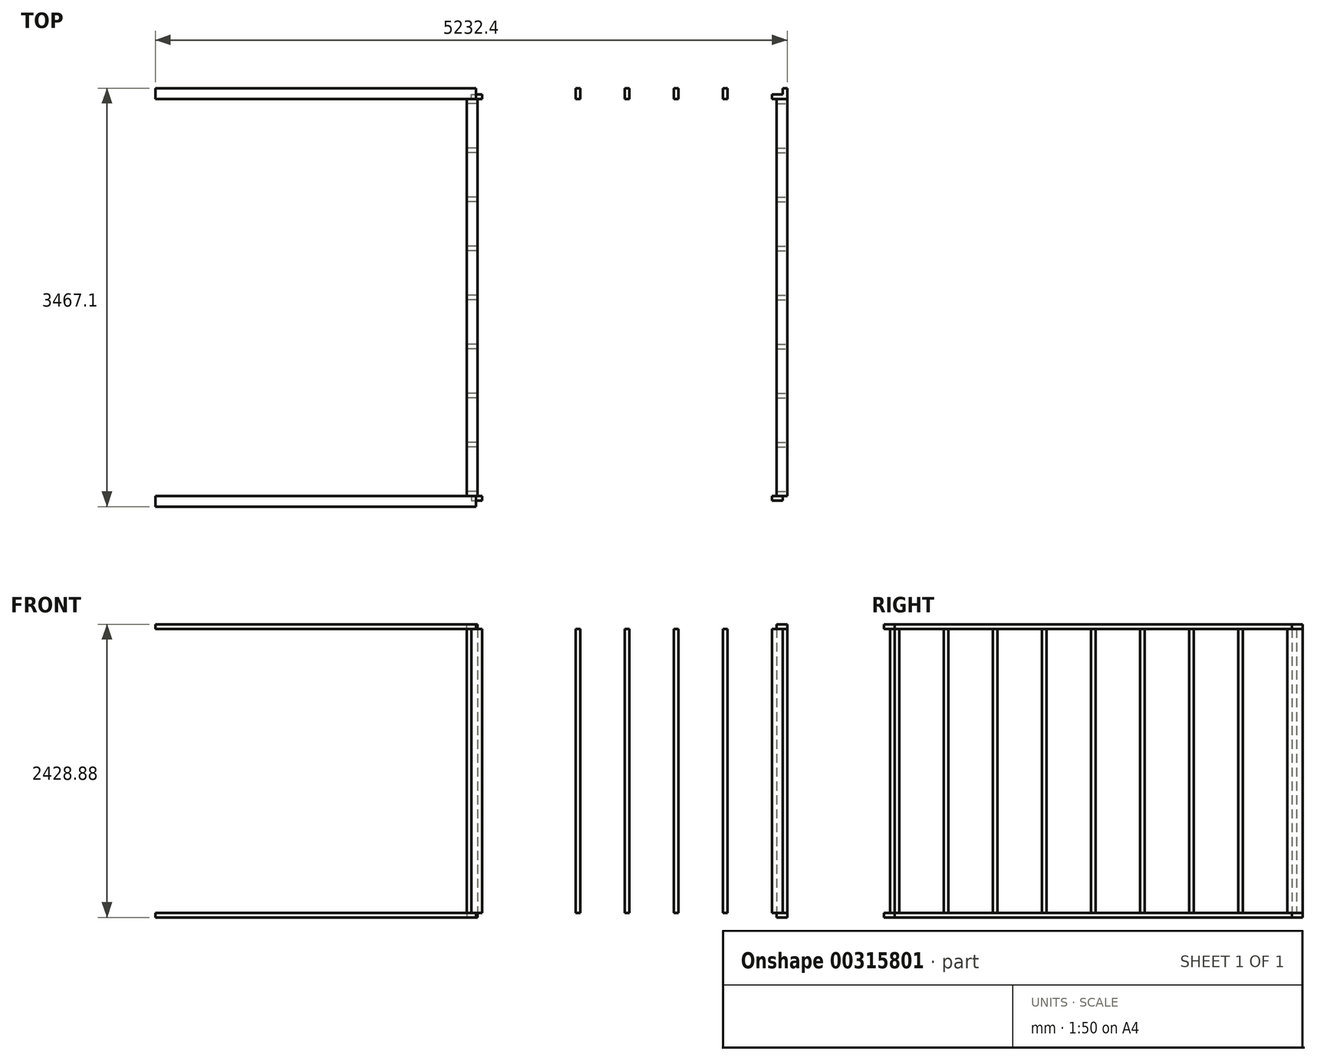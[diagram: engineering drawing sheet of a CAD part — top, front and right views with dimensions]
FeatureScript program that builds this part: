
annotation { "Feature Type Name" : "Feature", "Feature Type Description" : "" }
export const myFeature = defineFeature(function(context is Context, id is Id, definition is map)
    precondition{}
    {
        {
            var Q0;
            Q0=qCreatedBy(makeId("Top.planeOp"),FACE);
            var sketch = newSketch(context, id + "F0", { "sketchPlane" : qUnion([Q0])});
            skLineSegment(sketch, "E0.bottom", {"start": v(1238.25, -1644.65) * mm, "end": v(-1238.25, -1644.65) * mm});
            skLineSegment(sketch, "E0.top", {"start": v(1238.25, 1644.65) * mm, "end": v(-1238.25, 1644.65) * mm});
            skLineSegment(sketch, "E0.right", {"start": v(-1238.25, -1644.65) * mm, "end": v(-1238.25, 1644.65) * mm});
            skPoint(sketch, "E0.middle", {"position": v(0, 0) * mm});
            skLineSegment(sketch, "E1.bottom", {"start": v(-1238.25, 1644.65) * mm, "end": v(-1327.15, 1644.65) * mm});
            skLineSegment(sketch, "E1.top", {"start": v(-1238.25, 1606.55) * mm, "end": v(-1327.15, 1606.55) * mm});
            skLineSegment(sketch, "E1.left", {"start": v(-1238.25, 1644.65) * mm, "end": v(-1238.25, 1606.55) * mm});
            skLineSegment(sketch, "E1.right", {"start": v(-1327.15, 1644.65) * mm, "end": v(-1327.15, 1606.55) * mm});
            skLineSegment(sketch, "E2.1.0.0", {"start": v(-1238.25, 1238.25) * mm, "end": v(-1327.15, 1238.25) * mm});
            skLineSegment(sketch, "E2.1.0.1", {"start": v(-1238.25, 1238.25) * mm, "end": v(-1238.25, 1200.15) * mm});
            skLineSegment(sketch, "E2.1.0.2", {"start": v(-1238.25, 1200.15) * mm, "end": v(-1327.15, 1200.15) * mm});
            skLineSegment(sketch, "E2.1.0.3", {"start": v(-1327.15, 1238.25) * mm, "end": v(-1327.15, 1200.15) * mm});
            skLineSegment(sketch, "E2.2.0.0", {"start": v(-1238.25, 831.85) * mm, "end": v(-1327.15, 831.85) * mm});
            skLineSegment(sketch, "E2.2.0.1", {"start": v(-1238.25, 831.85) * mm, "end": v(-1238.25, 793.75) * mm});
            skLineSegment(sketch, "E2.2.0.2", {"start": v(-1238.25, 793.75) * mm, "end": v(-1327.15, 793.75) * mm});
            skLineSegment(sketch, "E2.2.0.3", {"start": v(-1327.15, 831.85) * mm, "end": v(-1327.15, 793.75) * mm});
            skLineSegment(sketch, "E2.3.0.0", {"start": v(-1238.25, 425.45) * mm, "end": v(-1327.15, 425.45) * mm});
            skLineSegment(sketch, "E2.3.0.1", {"start": v(-1238.25, 425.45) * mm, "end": v(-1238.25, 387.35) * mm});
            skLineSegment(sketch, "E2.3.0.2", {"start": v(-1238.25, 387.35) * mm, "end": v(-1327.15, 387.35) * mm});
            skLineSegment(sketch, "E2.3.0.3", {"start": v(-1327.15, 425.45) * mm, "end": v(-1327.15, 387.35) * mm});
            skLineSegment(sketch, "E2.4.0.0", {"start": v(-1238.25, 19.05) * mm, "end": v(-1327.15, 19.05) * mm});
            skLineSegment(sketch, "E2.4.0.1", {"start": v(-1238.25, 19.05) * mm, "end": v(-1238.25, -19.05) * mm});
            skLineSegment(sketch, "E2.4.0.2", {"start": v(-1238.25, -19.05) * mm, "end": v(-1327.15, -19.05) * mm});
            skLineSegment(sketch, "E2.4.0.3", {"start": v(-1327.15, 19.05) * mm, "end": v(-1327.15, -19.05) * mm});
            skLineSegment(sketch, "E2.5.0.0", {"start": v(-1238.25, -387.35) * mm, "end": v(-1327.15, -387.35) * mm});
            skLineSegment(sketch, "E2.5.0.1", {"start": v(-1238.25, -387.35) * mm, "end": v(-1238.25, -425.45) * mm});
            skLineSegment(sketch, "E2.5.0.2", {"start": v(-1238.25, -425.45) * mm, "end": v(-1327.15, -425.45) * mm});
            skLineSegment(sketch, "E2.5.0.3", {"start": v(-1327.15, -387.35) * mm, "end": v(-1327.15, -425.45) * mm});
            skLineSegment(sketch, "E2.6.0.0", {"start": v(-1238.25, -793.75) * mm, "end": v(-1327.15, -793.75) * mm});
            skLineSegment(sketch, "E2.6.0.1", {"start": v(-1238.25, -793.75) * mm, "end": v(-1238.25, -831.85) * mm});
            skLineSegment(sketch, "E2.6.0.2", {"start": v(-1238.25, -831.85) * mm, "end": v(-1327.15, -831.85) * mm});
            skLineSegment(sketch, "E2.6.0.3", {"start": v(-1327.15, -793.75) * mm, "end": v(-1327.15, -831.85) * mm});
            skLineSegment(sketch, "E2.7.0.0", {"start": v(-1238.25, -1200.15) * mm, "end": v(-1327.15, -1200.15) * mm});
            skLineSegment(sketch, "E2.7.0.1", {"start": v(-1238.25, -1200.15) * mm, "end": v(-1238.25, -1238.25) * mm});
            skLineSegment(sketch, "E2.7.0.2", {"start": v(-1238.25, -1238.25) * mm, "end": v(-1327.15, -1238.25) * mm});
            skLineSegment(sketch, "E2.7.0.3", {"start": v(-1327.15, -1200.15) * mm, "end": v(-1327.15, -1238.25) * mm});
            skLineSegment(sketch, "E2.8.0.0", {"start": v(-1238.25, -1606.55) * mm, "end": v(-1327.15, -1606.55) * mm});
            skLineSegment(sketch, "E2.8.0.1", {"start": v(-1238.25, -1606.55) * mm, "end": v(-1238.25, -1644.65) * mm});
            skLineSegment(sketch, "E2.8.0.2", {"start": v(-1238.25, -1644.65) * mm, "end": v(-1327.15, -1644.65) * mm});
            skLineSegment(sketch, "E2.8.0.3", {"start": v(-1327.15, -1606.55) * mm, "end": v(-1327.15, -1644.65) * mm});
            skLineSegment(sketch, "E2.direction1", {"start": v(-1327.15, 1644.65) * mm, "end": v(-1327.15, 1238.25) * mm, "construction": true});
            skLineSegment(sketch, "E3.bottom", {"start": v(-1327.15, -1644.65) * mm, "end": v(-1289.05, -1644.65) * mm});
            skLineSegment(sketch, "E3.top", {"start": v(-1327.15, -1733.55) * mm, "end": v(-1289.05, -1733.55) * mm});
            skLineSegment(sketch, "E3.left", {"start": v(-1327.15, -1644.65) * mm, "end": v(-1327.15, -1733.55) * mm});
            skLineSegment(sketch, "E3.right", {"start": v(-1289.05, -1644.65) * mm, "end": v(-1289.05, -1733.55) * mm});
            skLineSegment(sketch, "E4.bottom", {"start": v(-1289.05, -1644.65) * mm, "end": v(-1200.15, -1644.65) * mm});
            skLineSegment(sketch, "E4.top", {"start": v(-1289.05, -1682.75) * mm, "end": v(-1200.15, -1682.75) * mm});
            skLineSegment(sketch, "E4.left", {"start": v(-1289.05, -1644.65) * mm, "end": v(-1289.05, -1682.75) * mm});
            skLineSegment(sketch, "E4.right", {"start": v(-1200.15, -1644.65) * mm, "end": v(-1200.15, -1682.75) * mm});
            skLineSegment(sketch, "E5", {"start": v(-1289.05, -1644.65) * mm, "end": v(-882.65, -1644.65) * mm});
            skLineSegment(sketch, "E6", {"start": v(-1238.25, 1625.6) * mm, "end": v(-1238.25, -1625.6) * mm});
            skLineSegment(sketch, "E7.bottom", {"start": v(1238.25, 1644.65) * mm, "end": v(1327.15, 1644.65) * mm});
            skLineSegment(sketch, "E7.top", {"start": v(1238.25, 1606.55) * mm, "end": v(1327.15, 1606.55) * mm});
            skLineSegment(sketch, "E7.left", {"start": v(1238.25, 1644.65) * mm, "end": v(1238.25, 1606.55) * mm});
            skLineSegment(sketch, "E7.right", {"start": v(1327.15, 1644.65) * mm, "end": v(1327.15, 1606.55) * mm});
            skLineSegment(sketch, "E8.bottom", {"start": v(1238.25, -1644.65) * mm, "end": v(1327.15, -1644.65) * mm});
            skLineSegment(sketch, "E8.top", {"start": v(1238.25, -1606.55) * mm, "end": v(1327.15, -1606.55) * mm});
            skLineSegment(sketch, "E8.left", {"start": v(1238.25, -1644.65) * mm, "end": v(1238.25, -1606.55) * mm});
            skLineSegment(sketch, "E8.right", {"start": v(1327.15, -1644.65) * mm, "end": v(1327.15, -1606.55) * mm});
            skLineSegment(sketch, "E9.bottom", {"start": v(1327.15, -1644.65) * mm, "end": v(1289.05, -1644.65) * mm});
            skLineSegment(sketch, "E9.top", {"start": v(1327.15, -1733.55) * mm, "end": v(1289.05, -1733.55) * mm});
            skLineSegment(sketch, "E9.left", {"start": v(1327.15, -1644.65) * mm, "end": v(1327.15, -1733.55) * mm});
            skLineSegment(sketch, "E9.right", {"start": v(1289.05, -1644.65) * mm, "end": v(1289.05, -1733.55) * mm});
            skLineSegment(sketch, "E10.bottom", {"start": v(1289.05, -1644.65) * mm, "end": v(1200.15, -1644.65) * mm});
            skLineSegment(sketch, "E10.top", {"start": v(1289.05, -1682.75) * mm, "end": v(1200.15, -1682.75) * mm});
            skLineSegment(sketch, "E10.left", {"start": v(1289.05, -1644.65) * mm, "end": v(1289.05, -1682.75) * mm});
            skLineSegment(sketch, "E10.right", {"start": v(1200.15, -1644.65) * mm, "end": v(1200.15, -1682.75) * mm});
            skLineSegment(sketch, "E11", {"start": v(1289.05, -1644.65) * mm, "end": v(904.68, -1644.65) * mm});
            skLineSegment(sketch, "E12", {"start": v(904.68, -1644.65) * mm, "end": v(1289.05, -1644.65) * mm});
            skLineSegment(sketch, "E13.bottom", {"start": v(-1327.15, 1644.65) * mm, "end": v(-1289.05, 1644.65) * mm});
            skLineSegment(sketch, "E13.top", {"start": v(-1327.15, 1733.55) * mm, "end": v(-1289.05, 1733.55) * mm});
            skLineSegment(sketch, "E13.left", {"start": v(-1327.15, 1644.65) * mm, "end": v(-1327.15, 1733.55) * mm});
            skLineSegment(sketch, "E13.right", {"start": v(-1289.05, 1644.65) * mm, "end": v(-1289.05, 1733.55) * mm});
            skLineSegment(sketch, "E14.bottom", {"start": v(-1289.05, 1644.65) * mm, "end": v(-1200.15, 1644.65) * mm});
            skLineSegment(sketch, "E14.top", {"start": v(-1289.05, 1682.75) * mm, "end": v(-1200.15, 1682.75) * mm});
            skLineSegment(sketch, "E14.left", {"start": v(-1289.05, 1644.65) * mm, "end": v(-1289.05, 1682.75) * mm});
            skLineSegment(sketch, "E14.right", {"start": v(-1200.15, 1644.65) * mm, "end": v(-1200.15, 1682.75) * mm});
            skLineSegment(sketch, "E15", {"start": v(-1200.15, 1644.65) * mm, "end": v(-831.85, 1644.65) * mm});
            skLineSegment(sketch, "E16.bottom", {"start": v(-831.85, 1644.65) * mm, "end": v(-793.75, 1644.65) * mm});
            skLineSegment(sketch, "E16.top", {"start": v(-831.85, 1733.55) * mm, "end": v(-793.75, 1733.55) * mm});
            skLineSegment(sketch, "E16.left", {"start": v(-831.85, 1644.65) * mm, "end": v(-831.85, 1733.55) * mm});
            skLineSegment(sketch, "E16.right", {"start": v(-793.75, 1644.65) * mm, "end": v(-793.75, 1733.55) * mm});
            skLineSegment(sketch, "E17.1.0.0", {"start": v(-387.35, 1644.65) * mm, "end": v(-387.35, 1733.55) * mm});
            skLineSegment(sketch, "E17.1.0.1", {"start": v(-425.45, 1733.55) * mm, "end": v(-387.35, 1733.55) * mm});
            skLineSegment(sketch, "E17.1.0.2", {"start": v(-425.45, 1644.65) * mm, "end": v(-425.45, 1733.55) * mm});
            skLineSegment(sketch, "E17.2.0.0", {"start": v(19.05, 1644.65) * mm, "end": v(19.05, 1733.55) * mm});
            skLineSegment(sketch, "E17.2.0.1", {"start": v(-19.05, 1733.55) * mm, "end": v(19.05, 1733.55) * mm});
            skLineSegment(sketch, "E17.2.0.2", {"start": v(-19.05, 1644.65) * mm, "end": v(-19.05, 1733.55) * mm});
            skLineSegment(sketch, "E17.3.0.0", {"start": v(425.45, 1644.65) * mm, "end": v(425.45, 1733.55) * mm});
            skLineSegment(sketch, "E17.3.0.1", {"start": v(387.35, 1733.55) * mm, "end": v(425.45, 1733.55) * mm});
            skLineSegment(sketch, "E17.3.0.2", {"start": v(387.35, 1644.65) * mm, "end": v(387.35, 1733.55) * mm});
            skLineSegment(sketch, "E17.4.0.0", {"start": v(831.85, 1644.65) * mm, "end": v(831.85, 1733.55) * mm});
            skLineSegment(sketch, "E17.4.0.1", {"start": v(793.75, 1733.55) * mm, "end": v(831.85, 1733.55) * mm});
            skLineSegment(sketch, "E17.4.0.2", {"start": v(793.75, 1644.65) * mm, "end": v(793.75, 1733.55) * mm});
            skLineSegment(sketch, "E17.direction1", {"start": v(-793.75, 1644.65) * mm, "end": v(-387.35, 1644.65) * mm, "construction": true});
            skLineSegment(sketch, "E18.bottom", {"start": v(1327.15, 1644.65) * mm, "end": v(1282.7, 1644.65) * mm});
            skLineSegment(sketch, "E18.left", {"start": v(1327.15, 1644.65) * mm, "end": v(1327.15, 1733.55) * mm});
            skLineSegment(sketch, "E19", {"start": v(1327.15, 1733.55) * mm, "end": v(1289.05, 1733.55) * mm});
            skLineSegment(sketch, "E20", {"start": v(1289.05, 1733.55) * mm, "end": v(1289.05, 1644.65) * mm});
            skLineSegment(sketch, "E21", {"start": v(1289.05, 1644.65) * mm, "end": v(1327.15, 1644.65) * mm});
            skLineSegment(sketch, "E22.bottom", {"start": v(1289.05, 1644.65) * mm, "end": v(1200.15, 1644.65) * mm});
            skLineSegment(sketch, "E22.top", {"start": v(1289.05, 1682.75) * mm, "end": v(1200.15, 1682.75) * mm});
            skLineSegment(sketch, "E22.left", {"start": v(1289.05, 1644.65) * mm, "end": v(1289.05, 1682.75) * mm});
            skLineSegment(sketch, "E22.right", {"start": v(1200.15, 1644.65) * mm, "end": v(1200.15, 1682.75) * mm});
            skLineSegment(sketch, "E23", {"start": v(831.85, 1644.65) * mm, "end": v(1238.25, 1644.65) * mm});
            skLineSegment(sketch, "E24", {"start": v(1238.25, -1644.65) * mm, "end": v(1238.25, 1644.65) * mm});
            skLineSegment(sketch, "E25", {"start": v(0, 0) * mm, "end": v(0, 279.47) * mm});
            skLineSegment(sketch, "E26.MirrorCS", {"start": v(1327.15, 1238.25) * mm, "end": v(1327.15, 1200.15) * mm});
            skLineSegment(sketch, "E27.MirrorCS", {"start": v(1327.15, -793.75) * mm, "end": v(1327.15, -831.85) * mm});
            skLineSegment(sketch, "E28.MirrorCS", {"start": v(1327.15, 19.05) * mm, "end": v(1327.15, -19.05) * mm});
            skLineSegment(sketch, "E29.MirrorCS", {"start": v(1238.25, 793.75) * mm, "end": v(1327.15, 793.75) * mm});
            skLineSegment(sketch, "E30.MirrorCS", {"start": v(1327.15, 831.85) * mm, "end": v(1327.15, 793.75) * mm});
            skLineSegment(sketch, "E31.MirrorCS", {"start": v(1327.15, -387.35) * mm, "end": v(1327.15, -425.45) * mm});
            skLineSegment(sketch, "E32.MirrorCS", {"start": v(1238.25, 19.05) * mm, "end": v(1327.15, 19.05) * mm});
            skLineSegment(sketch, "E33.MirrorCS", {"start": v(1238.25, 831.85) * mm, "end": v(1238.25, 793.75) * mm});
            skLineSegment(sketch, "E34.MirrorCS", {"start": v(1238.25, -1200.15) * mm, "end": v(1327.15, -1200.15) * mm});
            skLineSegment(sketch, "E35.MirrorCS", {"start": v(1238.25, -793.75) * mm, "end": v(1238.25, -831.85) * mm});
            skLineSegment(sketch, "E36.MirrorCS", {"start": v(1238.25, 425.45) * mm, "end": v(1327.15, 425.45) * mm});
            skLineSegment(sketch, "E37.MirrorCS", {"start": v(1238.25, 1238.25) * mm, "end": v(1327.15, 1238.25) * mm});
            skLineSegment(sketch, "E38.MirrorCS", {"start": v(1238.25, 1238.25) * mm, "end": v(1238.25, 1200.15) * mm});
            skLineSegment(sketch, "E39.MirrorCS", {"start": v(1238.25, 387.35) * mm, "end": v(1327.15, 387.35) * mm});
            skLineSegment(sketch, "E40.MirrorCS", {"start": v(1238.25, 1200.15) * mm, "end": v(1327.15, 1200.15) * mm});
            skLineSegment(sketch, "E41.MirrorCS", {"start": v(1238.25, -387.35) * mm, "end": v(1238.25, -425.45) * mm});
            skLineSegment(sketch, "E42.MirrorCS", {"start": v(1238.25, -1200.15) * mm, "end": v(1238.25, -1238.25) * mm});
            skLineSegment(sketch, "E43.MirrorCS", {"start": v(1238.25, -793.75) * mm, "end": v(1327.15, -793.75) * mm});
            skLineSegment(sketch, "E44.MirrorCS", {"start": v(1238.25, -1238.25) * mm, "end": v(1327.15, -1238.25) * mm});
            skLineSegment(sketch, "E45.MirrorCS", {"start": v(1238.25, -19.05) * mm, "end": v(1327.15, -19.05) * mm});
            skLineSegment(sketch, "E46.MirrorCS", {"start": v(1238.25, 831.85) * mm, "end": v(1327.15, 831.85) * mm});
            skLineSegment(sketch, "E47.MirrorCS", {"start": v(1238.25, -387.35) * mm, "end": v(1327.15, -387.35) * mm});
            skLineSegment(sketch, "E48.MirrorCS", {"start": v(1238.25, -831.85) * mm, "end": v(1327.15, -831.85) * mm});
            skLineSegment(sketch, "E49.MirrorCS", {"start": v(1238.25, 425.45) * mm, "end": v(1238.25, 387.35) * mm});
            skLineSegment(sketch, "E50.MirrorCS", {"start": v(1327.15, 425.45) * mm, "end": v(1327.15, 387.35) * mm});
            skLineSegment(sketch, "E51.MirrorCS", {"start": v(1238.25, 19.05) * mm, "end": v(1238.25, -19.05) * mm});
            skLineSegment(sketch, "E52.MirrorCS", {"start": v(1327.15, -1200.15) * mm, "end": v(1327.15, -1238.25) * mm});
            skLineSegment(sketch, "E53.MirrorCS", {"start": v(1238.25, -425.45) * mm, "end": v(1327.15, -425.45) * mm});
            skSolve(sketch);
        }
        {
            var Q0;
            {var subQ1=sQuery(id+"F0.wireOp",EDGE,"E1.top");Q0=makeQuery(id+"F0.imprint","IMPRINT",FACE,{"disambiguationData":[TD([[makeQuery(id+"F0.imprint","IMPRINT",EDGE,{"derivedFrom":subQ1}),-1.0]])]});}
            var Q1;
            Q1=makeQuery(id+"F0.imprint","IMPRINT",FACE,{"disambiguationData":[TD([[makeQuery(id+"F0.imprint","IMPRINT",EDGE,{"derivedFrom":sQuery(id+"F0.wireOp",EDGE,"E13.bottom")}),1.0]])]});
            var Q2;
            Q2=makeQuery(id+"F0.imprint","IMPRINT",FACE,{"disambiguationData":[TD([[makeQuery(id+"F0.imprint","IMPRINT",EDGE,{"derivedFrom":sQuery(id+"F0.wireOp",EDGE,"E14.top")}),-1.0]])]});
            var Q3;
            Q3=makeQuery(id+"F0.imprint","IMPRINT",FACE,{"disambiguationData":[TD([[makeQuery(id+"F0.imprint","IMPRINT",EDGE,{"derivedFrom":sQuery(id+"F0.wireOp",EDGE,"E16.bottom")}),1.0]])]});
            var Q4;
            {var subQ0=sQuery(id+"F0.wireOp",EDGE,"E17.1.0.0");Q4=makeQuery(id+"F0.imprint","IMPRINT",FACE,{"disambiguationData":[TD([[makeQuery(id+"F0.imprint","IMPRINT",EDGE,{"derivedFrom":subQ0}),1.0]])]});}
            var Q5;
            {var subQ0=sQuery(id+"F0.wireOp",EDGE,"E17.2.0.0");Q5=makeQuery(id+"F0.imprint","IMPRINT",FACE,{"disambiguationData":[TD([[makeQuery(id+"F0.imprint","IMPRINT",EDGE,{"derivedFrom":subQ0}),1.0]])]});}
            var Q6;
            {var subQ0=sQuery(id+"F0.wireOp",EDGE,"E17.3.0.0");Q6=makeQuery(id+"F0.imprint","IMPRINT",FACE,{"disambiguationData":[TD([[makeQuery(id+"F0.imprint","IMPRINT",EDGE,{"derivedFrom":subQ0}),1.0]])]});}
            var Q7;
            Q7=makeQuery(id+"F0.imprint","IMPRINT",FACE,{"disambiguationData":[TD([[makeQuery(id+"F0.imprint","IMPRINT",EDGE,{"derivedFrom":sQuery(id+"F0.wireOp",EDGE,"E22.top")}),1.0]])]});
            var Q8;
            Q8=makeQuery(id+"F0.imprint","IMPRINT",FACE,{"disambiguationData":[TD([[makeQuery(id+"F0.imprint","IMPRINT",EDGE,{"derivedFrom":sQuery(id+"F0.wireOp",EDGE,"E18.left")}),1.0]])]});
            var Q9;
            {var subQ3=sQuery(id+"F0.wireOp",EDGE,"E7.top");Q9=makeQuery(id+"F0.imprint","IMPRINT",FACE,{"disambiguationData":[TD([[makeQuery(id+"F0.imprint","IMPRINT",EDGE,{"derivedFrom":subQ3}),1.0]])]});}
            var Q10;
            Q10=makeQuery(id+"F0.imprint","IMPRINT",FACE,{"disambiguationData":[TD([[makeQuery(id+"F0.imprint","IMPRINT",EDGE,{"derivedFrom":sQuery(id+"F0.wireOp",EDGE,"E26.MirrorCS")}),-1.0]])]});
            var Q11;
            Q11=makeQuery(id+"F0.imprint","IMPRINT",FACE,{"disambiguationData":[TD([[makeQuery(id+"F0.imprint","IMPRINT",EDGE,{"derivedFrom":sQuery(id+"F0.wireOp",EDGE,"E29.MirrorCS")}),1.0]])]});
            var Q12;
            Q12=makeQuery(id+"F0.imprint","IMPRINT",FACE,{"disambiguationData":[TD([[makeQuery(id+"F0.imprint","IMPRINT",EDGE,{"derivedFrom":sQuery(id+"F0.wireOp",EDGE,"E36.MirrorCS")}),-1.0]])]});
            var Q13;
            Q13=makeQuery(id+"F0.imprint","IMPRINT",FACE,{"disambiguationData":[TD([[makeQuery(id+"F0.imprint","IMPRINT",EDGE,{"derivedFrom":sQuery(id+"F0.wireOp",EDGE,"E28.MirrorCS")}),-1.0]])]});
            var Q14;
            Q14=makeQuery(id+"F0.imprint","IMPRINT",FACE,{"disambiguationData":[TD([[makeQuery(id+"F0.imprint","IMPRINT",EDGE,{"derivedFrom":sQuery(id+"F0.wireOp",EDGE,"E31.MirrorCS")}),-1.0]])]});
            var Q15;
            Q15=makeQuery(id+"F0.imprint","IMPRINT",FACE,{"disambiguationData":[TD([[makeQuery(id+"F0.imprint","IMPRINT",EDGE,{"derivedFrom":sQuery(id+"F0.wireOp",EDGE,"E27.MirrorCS")}),-1.0]])]});
            var Q16;
            Q16=makeQuery(id+"F0.imprint","IMPRINT",FACE,{"disambiguationData":[TD([[makeQuery(id+"F0.imprint","IMPRINT",EDGE,{"derivedFrom":sQuery(id+"F0.wireOp",EDGE,"E34.MirrorCS")}),-1.0]])]});
            var Q17;
            {var subQ4=sQuery(id+"F0.wireOp",EDGE,"E8.top");Q17=makeQuery(id+"F0.imprint","IMPRINT",FACE,{"disambiguationData":[TD([[makeQuery(id+"F0.imprint","IMPRINT",EDGE,{"derivedFrom":subQ4}),-1.0]])]});}
            var Q18;
            Q18=makeQuery(id+"F0.imprint","IMPRINT",FACE,{"disambiguationData":[TD([[makeQuery(id+"F0.imprint","IMPRINT",EDGE,{"derivedFrom":sQuery(id+"F0.wireOp",EDGE,"E10.top")}),-1.0]])]});
            var Q19;
            Q19=makeQuery(id+"F0.imprint","IMPRINT",FACE,{"disambiguationData":[TD([[makeQuery(id+"F0.imprint","IMPRINT",EDGE,{"derivedFrom":sQuery(id+"F0.wireOp",EDGE,"E9.bottom")}),1.0]])]});
            var Q20;
            Q20=makeQuery(id+"F0.imprint","IMPRINT",FACE,{"disambiguationData":[TD([[makeQuery(id+"F0.imprint","IMPRINT",EDGE,{"derivedFrom":sQuery(id+"F0.wireOp",EDGE,"E4.top")}),1.0]])]});
            var Q21;
            Q21=makeQuery(id+"F0.imprint","IMPRINT",FACE,{"disambiguationData":[TD([[makeQuery(id+"F0.imprint","IMPRINT",EDGE,{"derivedFrom":sQuery(id+"F0.wireOp",EDGE,"E3.bottom")}),-1.0]])]});
            var Q22;
            {var subQ3=sQuery(id+"F0.wireOp",EDGE,"E2.8.0.0");Q22=makeQuery(id+"F0.imprint","IMPRINT",FACE,{"disambiguationData":[TD([[makeQuery(id+"F0.imprint","IMPRINT",EDGE,{"derivedFrom":subQ3}),1.0]])]});}
            var Q23;
            {var subQ0=sQuery(id+"F0.wireOp",EDGE,"E2.7.0.0");Q23=makeQuery(id+"F0.imprint","IMPRINT",FACE,{"disambiguationData":[TD([[makeQuery(id+"F0.imprint","IMPRINT",EDGE,{"derivedFrom":subQ0}),1.0]])]});}
            var Q24;
            {var subQ0=sQuery(id+"F0.wireOp",EDGE,"E2.6.0.0");Q24=makeQuery(id+"F0.imprint","IMPRINT",FACE,{"disambiguationData":[TD([[makeQuery(id+"F0.imprint","IMPRINT",EDGE,{"derivedFrom":subQ0}),1.0]])]});}
            var Q25;
            {var subQ0=sQuery(id+"F0.wireOp",EDGE,"E2.5.0.0");Q25=makeQuery(id+"F0.imprint","IMPRINT",FACE,{"disambiguationData":[TD([[makeQuery(id+"F0.imprint","IMPRINT",EDGE,{"derivedFrom":subQ0}),1.0]])]});}
            var Q26;
            {var subQ0=sQuery(id+"F0.wireOp",EDGE,"E2.4.0.0");Q26=makeQuery(id+"F0.imprint","IMPRINT",FACE,{"disambiguationData":[TD([[makeQuery(id+"F0.imprint","IMPRINT",EDGE,{"derivedFrom":subQ0}),1.0]])]});}
            var Q27;
            {var subQ0=sQuery(id+"F0.wireOp",EDGE,"E2.3.0.0");Q27=makeQuery(id+"F0.imprint","IMPRINT",FACE,{"disambiguationData":[TD([[makeQuery(id+"F0.imprint","IMPRINT",EDGE,{"derivedFrom":subQ0}),1.0]])]});}
            var Q28;
            {var subQ0=sQuery(id+"F0.wireOp",EDGE,"E2.2.0.0");Q28=makeQuery(id+"F0.imprint","IMPRINT",FACE,{"disambiguationData":[TD([[makeQuery(id+"F0.imprint","IMPRINT",EDGE,{"derivedFrom":subQ0}),1.0]])]});}
            var Q29;
            {var subQ0=sQuery(id+"F0.wireOp",EDGE,"E2.1.0.0");Q29=makeQuery(id+"F0.imprint","IMPRINT",FACE,{"disambiguationData":[TD([[makeQuery(id+"F0.imprint","IMPRINT",EDGE,{"derivedFrom":subQ0}),1.0]])]});}
            var Q30;
            {var subQ0=sQuery(id+"F0.wireOp",EDGE,"E17.4.0.0");Q30=makeQuery(id+"F0.imprint","IMPRINT",FACE,{"disambiguationData":[TD([[makeQuery(id+"F0.imprint","IMPRINT",EDGE,{"derivedFrom":subQ0}),1.0]])]});}
            extrude(context, id + "F1", {"entities" : qUnion([Q0, Q1, Q2, Q3, Q4, Q5, Q6, Q7, Q8, Q9, Q10, Q11, Q12, Q13, Q14, Q15, Q16, Q17, Q18, Q19, Q20, Q21, Q22, Q23, Q24, Q25, Q26, Q27, Q28, Q29, Q30]), "depth" : 2352.67 * mm});
        }
        {
            var Q0;
            Q0=makeQuery(id+"F1.opExtrude","SWEPT_FACE",FACE,{"disambiguationData":[OSD([sQuery(id+"F0.wireOp",EDGE,"E8.top")])]});
            var sketch = newSketch(context, id + "F2", { "sketchPlane" : qUnion([Q0])});
            skLineSegment(sketch, "E54.bottom", {"start": v(-1327.15, 0) * mm, "end": v(-1238.25, 0) * mm});
            skLineSegment(sketch, "E54.top", {"start": v(-1327.15, -38.1) * mm, "end": v(-1238.25, -38.1) * mm});
            skLineSegment(sketch, "E54.left", {"start": v(-1327.15, 0) * mm, "end": v(-1327.15, -38.1) * mm});
            skLineSegment(sketch, "E54.right", {"start": v(-1238.25, 0) * mm, "end": v(-1238.25, -38.1) * mm});
            skSolve(sketch);
        }
        {
            var Q0;
            Q0=makeQuery(id+"F2.imprint","IMPRINT",FACE,{"disambiguationData":[TD([[makeQuery(id+"F2.imprint","IMPRINT",EDGE,{"derivedFrom":sQuery(id+"F2.wireOp",EDGE,"E54.bottom")}),1.0]])]});
            extrude(context, id + "F3", {"entities" : qUnion([Q0]), "depth" : 3251.2 * mm, "hasSecondDirection" : true, "secondDirectionOppositeDirection" : true, "secondDirectionDepth" : 38.1 * mm});
        }
        {
            var Q0;
            Q0=makeQuery(id+"F1.opExtrude","SWEPT_FACE",FACE,{"disambiguationData":[OSD([sQuery(id+"F0.wireOp",EDGE,"E1.top")])]});
            var sketch = newSketch(context, id + "F4", { "sketchPlane" : qUnion([Q0])});
            skLineSegment(sketch, "E55.bottom", {"start": v(-1327.15, 0) * mm, "end": v(-1238.25, 0) * mm});
            skLineSegment(sketch, "E55.top", {"start": v(-1327.15, -38.1) * mm, "end": v(-1238.25, -38.1) * mm});
            skLineSegment(sketch, "E55.left", {"start": v(-1327.15, 0) * mm, "end": v(-1327.15, -38.1) * mm});
            skLineSegment(sketch, "E55.right", {"start": v(-1238.25, 0) * mm, "end": v(-1238.25, -38.1) * mm});
            skSolve(sketch);
        }
        {
            var Q0;
            Q0=makeQuery(id+"F4.imprint","IMPRINT",FACE,{"disambiguationData":[TD([[makeQuery(id+"F4.imprint","IMPRINT",EDGE,{"derivedFrom":sQuery(id+"F4.wireOp",EDGE,"E55.bottom")}),1.0]])]});
            extrude(context, id + "F5", {"entities" : qUnion([Q0]), "depth" : 3251.2 * mm, "hasSecondDirection" : true, "secondDirectionOppositeDirection" : true, "secondDirectionDepth" : 38.1 * mm});
        }
        {
            var Q0;
            Q0=makeQuery(id+"F1.opExtrude","SWEPT_FACE",FACE,{"disambiguationData":[OSD([sQuery(id+"F0.wireOp",EDGE,"E3.right")])]});
            var sketch = newSketch(context, id + "F6", { "sketchPlane" : qUnion([Q0])});
            skLineSegment(sketch, "E56.bottom", {"start": v(-1733.55, 0) * mm, "end": v(-1644.65, 0) * mm});
            skLineSegment(sketch, "E56.top", {"start": v(-1733.55, -38.1) * mm, "end": v(-1644.65, -38.1) * mm});
            skLineSegment(sketch, "E56.left", {"start": v(-1733.55, 0) * mm, "end": v(-1733.55, -38.1) * mm});
            skLineSegment(sketch, "E56.right", {"start": v(-1644.65, 0) * mm, "end": v(-1644.65, -38.1) * mm});
            skSolve(sketch);
        }
        {
            var Q0;
            Q0=makeQuery(id+"F6.imprint","IMPRINT",FACE,{"disambiguationData":[TD([[makeQuery(id+"F6.imprint","IMPRINT",EDGE,{"derivedFrom":sQuery(id+"F6.wireOp",EDGE,"E56.top")}),1.0]])]});
            extrude(context, id + "F7", {"entities" : qUnion([Q0]), "depth" : 2616.2 * mm, "hasSecondDirection" : true, "secondDirectionOppositeDirection" : true, "secondDirectionDepth" : 38.1 * mm});
        }
        {
            var Q0;
            Q0=makeQuery(id+"F1.opExtrude","SWEPT_FACE",FACE,{"disambiguationData":[OSD([sQuery(id+"F0.wireOp",EDGE,"E13.right")])]});
            var sketch = newSketch(context, id + "F8", { "sketchPlane" : qUnion([Q0])});
            skLineSegment(sketch, "E57.bottom", {"start": v(1733.55, 0) * mm, "end": v(1644.65, 0) * mm});
            skLineSegment(sketch, "E57.top", {"start": v(1733.55, -38.1) * mm, "end": v(1644.65, -38.1) * mm});
            skLineSegment(sketch, "E57.left", {"start": v(1733.55, 0) * mm, "end": v(1733.55, -38.1) * mm});
            skLineSegment(sketch, "E57.right", {"start": v(1644.65, 0) * mm, "end": v(1644.65, -38.1) * mm});
            skSolve(sketch);
        }
        {
            var Q0;
            Q0=makeQuery(id+"F8.imprint","IMPRINT",FACE,{"disambiguationData":[TD([[makeQuery(id+"F8.imprint","IMPRINT",EDGE,{"derivedFrom":sQuery(id+"F8.wireOp",EDGE,"E57.top")}),-1.0]])]});
            extrude(context, id + "F9", {"entities" : qUnion([Q0]), "depth" : 2616.2 * mm, "hasSecondDirection" : true, "secondDirectionOppositeDirection" : true, "secondDirectionDepth" : 38.1 * mm});
        }
        {
            var Q0;
            Q0=makeQuery(id+"F1.opExtrude","SWEPT_FACE",FACE,{"disambiguationData":[OSD([sQuery(id+"F0.wireOp",EDGE,"E7.top")])]});
            var sketch = newSketch(context, id + "F10", { "sketchPlane" : qUnion([Q0])});
            skLineSegment(sketch, "E58.bottom", {"start": v(1238.25, 2352.68) * mm, "end": v(1327.15, 2352.68) * mm});
            skLineSegment(sketch, "E58.top", {"start": v(1238.25, 2390.78) * mm, "end": v(1327.15, 2390.78) * mm});
            skLineSegment(sketch, "E58.left", {"start": v(1238.25, 2352.68) * mm, "end": v(1238.25, 2390.78) * mm});
            skLineSegment(sketch, "E58.right", {"start": v(1327.15, 2352.68) * mm, "end": v(1327.15, 2390.78) * mm});
            skSolve(sketch);
        }
        {
            var Q0;
            Q0=makeQuery(id+"F10.imprint","IMPRINT",FACE,{"disambiguationData":[TD([[makeQuery(id+"F10.imprint","IMPRINT",EDGE,{"derivedFrom":sQuery(id+"F10.wireOp",EDGE,"E58.bottom")}),1.0]])]});
            extrude(context, id + "F11", {"entities" : qUnion([Q0]), "depth" : 3251.2 * mm, "hasSecondDirection" : true, "secondDirectionOppositeDirection" : true, "secondDirectionDepth" : 38.1 * mm});
        }
        {
            var Q0;
            Q0=makeQuery(id+"F1.opExtrude","SWEPT_FACE",FACE,{"disambiguationData":[OSD([sQuery(id+"F0.wireOp",EDGE,"E1.top")])]});
            var sketch = newSketch(context, id + "F12", { "sketchPlane" : qUnion([Q0])});
            skLineSegment(sketch, "E59.bottom", {"start": v(-1327.15, 2352.68) * mm, "end": v(-1238.25, 2352.68) * mm});
            skLineSegment(sketch, "E59.top", {"start": v(-1327.15, 2390.78) * mm, "end": v(-1238.25, 2390.78) * mm});
            skLineSegment(sketch, "E59.left", {"start": v(-1327.15, 2352.68) * mm, "end": v(-1327.15, 2390.78) * mm});
            skLineSegment(sketch, "E59.right", {"start": v(-1238.25, 2352.68) * mm, "end": v(-1238.25, 2390.78) * mm});
            skSolve(sketch);
        }
        {
            var Q0;
            Q0=makeQuery(id+"F12.imprint","IMPRINT",FACE,{"disambiguationData":[TD([[makeQuery(id+"F12.imprint","IMPRINT",EDGE,{"derivedFrom":sQuery(id+"F12.wireOp",EDGE,"E59.bottom")}),-1.0]])]});
            extrude(context, id + "F13", {"entities" : qUnion([Q0]), "depth" : 3251.2 * mm, "hasSecondDirection" : true, "secondDirectionOppositeDirection" : true, "secondDirectionDepth" : 38.1 * mm});
        }
        {
            var Q0;
            Q0=makeQuery(id+"F1.opExtrude","SWEPT_FACE",FACE,{"disambiguationData":[OSD([sQuery(id+"F0.wireOp",EDGE,"E3.right")])]});
            var sketch = newSketch(context, id + "F14", { "sketchPlane" : qUnion([Q0])});
            skLineSegment(sketch, "E60.bottom", {"start": v(-1733.55, 2352.68) * mm, "end": v(-1644.65, 2352.68) * mm});
            skLineSegment(sketch, "E60.top", {"start": v(-1733.55, 2390.78) * mm, "end": v(-1644.65, 2390.78) * mm});
            skLineSegment(sketch, "E60.left", {"start": v(-1733.55, 2352.68) * mm, "end": v(-1733.55, 2390.78) * mm});
            skLineSegment(sketch, "E60.right", {"start": v(-1644.65, 2352.68) * mm, "end": v(-1644.65, 2390.78) * mm});
            skSolve(sketch);
        }
        {
            var Q0;
            Q0=makeQuery(id+"F14.imprint","IMPRINT",FACE,{"disambiguationData":[TD([[makeQuery(id+"F14.imprint","IMPRINT",EDGE,{"derivedFrom":sQuery(id+"F14.wireOp",EDGE,"E60.top")}),-1.0]])]});
            extrude(context, id + "F15", {"entities" : qUnion([Q0]), "depth" : 2616.2 * mm, "hasSecondDirection" : true, "secondDirectionOppositeDirection" : true, "secondDirectionDepth" : 38.1 * mm});
        }
        {
            var Q0;
            Q0=makeQuery(id+"F1.opExtrude","SWEPT_FACE",FACE,{"disambiguationData":[OSD([sQuery(id+"F0.wireOp",EDGE,"E13.right")])]});
            var sketch = newSketch(context, id + "F16", { "sketchPlane" : qUnion([Q0])});
            skLineSegment(sketch, "E61.bottom", {"start": v(1733.55, 2352.68) * mm, "end": v(1644.65, 2352.68) * mm});
            skLineSegment(sketch, "E61.top", {"start": v(1733.55, 2390.78) * mm, "end": v(1644.65, 2390.78) * mm});
            skLineSegment(sketch, "E61.left", {"start": v(1733.55, 2352.68) * mm, "end": v(1733.55, 2390.78) * mm});
            skLineSegment(sketch, "E61.right", {"start": v(1644.65, 2352.68) * mm, "end": v(1644.65, 2390.78) * mm});
            skSolve(sketch);
        }
        {
            var Q0;
            Q0 = qSketchRegion(id + "F16", true);
            extrude(context, id + "F17", {"entities" : qUnion([Q0]), "depth" : 2616.2 * mm, "hasSecondDirection" : true, "secondDirectionOppositeDirection" : true, "secondDirectionDepth" : 38.1 * mm});
        }
    });
